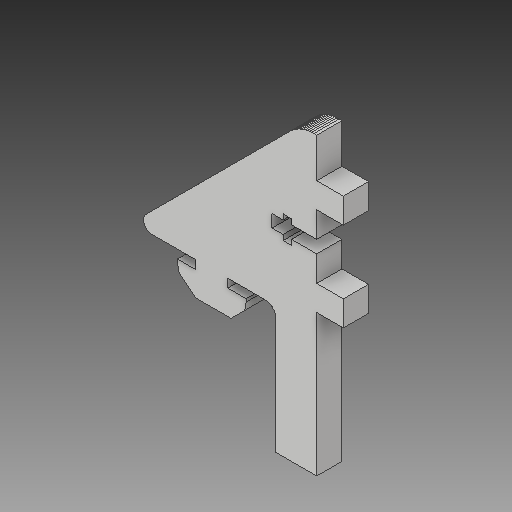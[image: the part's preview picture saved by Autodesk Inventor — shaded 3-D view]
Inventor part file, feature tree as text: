
AUTODESK INVENTOR PART (.ipt)
format: ipt  version: 2018 (Build 220112000, 112)  size: 368,640 bytes
history: native  units: mm
features: other x3, sketch x1
ambient origin geometry x8: Origin, YZ Plane, XZ Plane, XY Plane, X Axis, Y Axis, Z Axis, Center Point
bodies: Solid1 (feature_tree)
feature tree (4):
  other  "Y-Motor-Brace.ipt"
  other  "Solid1::Y-Motor-Brace.ipt"
  other  "TaggingFeature1"
  sketch  "Sketch1"  dims[d0=10.0mm]
